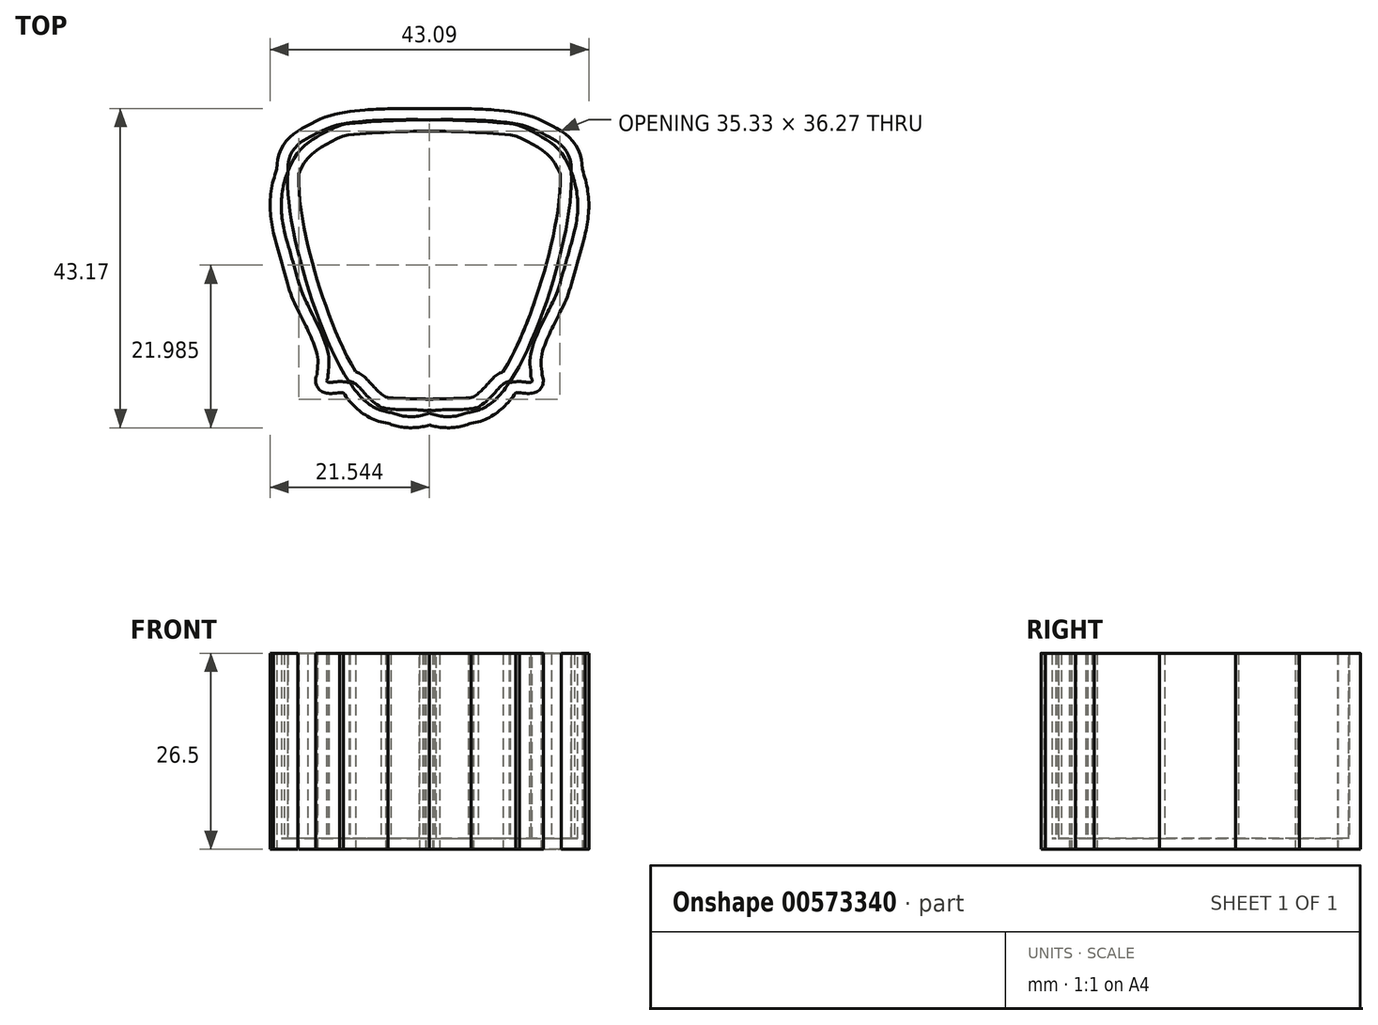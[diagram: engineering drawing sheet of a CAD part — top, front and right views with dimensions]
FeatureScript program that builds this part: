
annotation { "Feature Type Name" : "Feature", "Feature Type Description" : "" }
export const myFeature = defineFeature(function(context is Context, id is Id, definition is map)
    precondition{}
    {
        {
            var Q0;
            Q0=qCreatedBy(makeId("Top.planeOp"),FACE);
            var sketch = newSketch(context, id + "F0", { "sketchPlane" : qUnion([Q0])});
            skPoint(sketch, "E0", {"position": v(3.41, -16.1) * mm});
            skFitSpline(sketch, "E1", {"points": [v(19.25, -23.79) * mm, v(20.6, -21.15) * mm, v(22, -16.48) * mm, v(23.43, -9.07) * mm, v(21.24, -2.26) * mm, v(18.55, -0.04) * mm, v(16.06, 1.32) * mm, v(12.81, 1.87) * mm, v(-7.37, 1.93) * mm, v(-12.55, 0.1) * mm, v(-15.74, -4.2) * mm, v(2.7, -37.03) * mm, v(11.82, -35.05) * mm, v(14.26, -33.06) * mm, v(17.26, -33.1) * mm, v(16.57, -30.92) * mm, v(19.25, -23.79) * mm]});
            skFitSpline(sketch, "E2", {"points": [v(19.15, -24.22) * mm, v(20.57, -21) * mm, v(21.95, -16.45) * mm, v(23.46, -9.07) * mm, v(21.3, -2.27) * mm, v(18.6, 0.01) * mm, v(15.9, 1.4) * mm, v(12.77, 1.93) * mm, v(-7.36, 1.91) * mm, v(-12.59, 0.02) * mm, v(-15.67, -4.13) * mm, v(-5.73, -35.3) * mm, v(2.68, -37) * mm, v(10.02, -36.54) * mm, v(11.8, -35.1) * mm, v(14.33, -33.21) * mm, v(16.97, -32.83) * mm, v(17, -30.19) * mm, v(19.15, -24.22) * mm]});
            skFitSpline(sketch, "E3.MirrorCS", {"points": [v(-12.32, -24.22) * mm, v(-13.74, -21) * mm, v(-15.12, -16.45) * mm, v(-16.64, -9.07) * mm, v(-14.48, -2.27) * mm, v(-11.77, 0.01) * mm, v(-9.08, 1.4) * mm, v(-5.94, 1.93) * mm, v(14.19, 1.91) * mm, v(19.42, 0.02) * mm, v(22.5, -4.13) * mm, v(12.56, -35.3) * mm, v(4.14, -37) * mm, v(-3.2, -36.54) * mm, v(-4.97, -35.1) * mm, v(-7.5, -33.21) * mm, v(-10.14, -32.83) * mm, v(-10.17, -30.19) * mm, v(-12.32, -24.22) * mm]});
            skFitSpline(sketch, "E4.MirrorCS", {"points": [v(-12.42, -23.79) * mm, v(-13.78, -21.15) * mm, v(-15.17, -16.48) * mm, v(-16.6, -9.07) * mm, v(-14.42, -2.26) * mm, v(-11.72, -0.04) * mm, v(-9.23, 1.32) * mm, v(-5.99, 1.87) * mm, v(14.2, 1.93) * mm, v(19.38, 0.1) * mm, v(22.56, -4.2) * mm, v(4.13, -37.03) * mm, v(-5, -35.05) * mm, v(-7.44, -33.06) * mm, v(-10.43, -33.1) * mm, v(-9.74, -30.92) * mm, v(-12.42, -23.79) * mm]});
            skSolve(sketch);
        }
        {
            var Q0;
            Q0 = qSketchRegion(id + "F0", true);
            extrude(context, id + "F1", {"entities" : qUnion([Q0]), "depth" : 25 * mm, "offsetDistance" : 25 * mm});
        }
        {
            var Q0;
            Q0=makeQuery(id+"F1.opExtrude","CAP_FACE",FACE,{"disambiguationData":[OSD([sQuery(id+"F0.wireOp",EDGE,"E1"),sQuery(id+"F0.wireOp",EDGE,"E2"),sQuery(id+"F0.wireOp",EDGE,"E3.MirrorCS"),sQuery(id+"F0.wireOp",EDGE,"E4.MirrorCS")])],"isStart":false});
            var Q1;
            Q1=makeQuery(id+"F1.opExtrude","SWEPT_BODY",BODY,{"disambiguationData":[OSD([sQuery(id+"F0.wireOp",EDGE,"E1"),sQuery(id+"F0.wireOp",EDGE,"E2"),sQuery(id+"F0.wireOp",EDGE,"E3.MirrorCS"),sQuery(id+"F0.wireOp",EDGE,"E4.MirrorCS")])]});
            shell(context, id + "F2", {"entities" : qUnion([Q0]), "parts" : qUnion([Q1]), "thickness" : 1.5 * mm, "oppositeDirection" : true});
        }
    });
